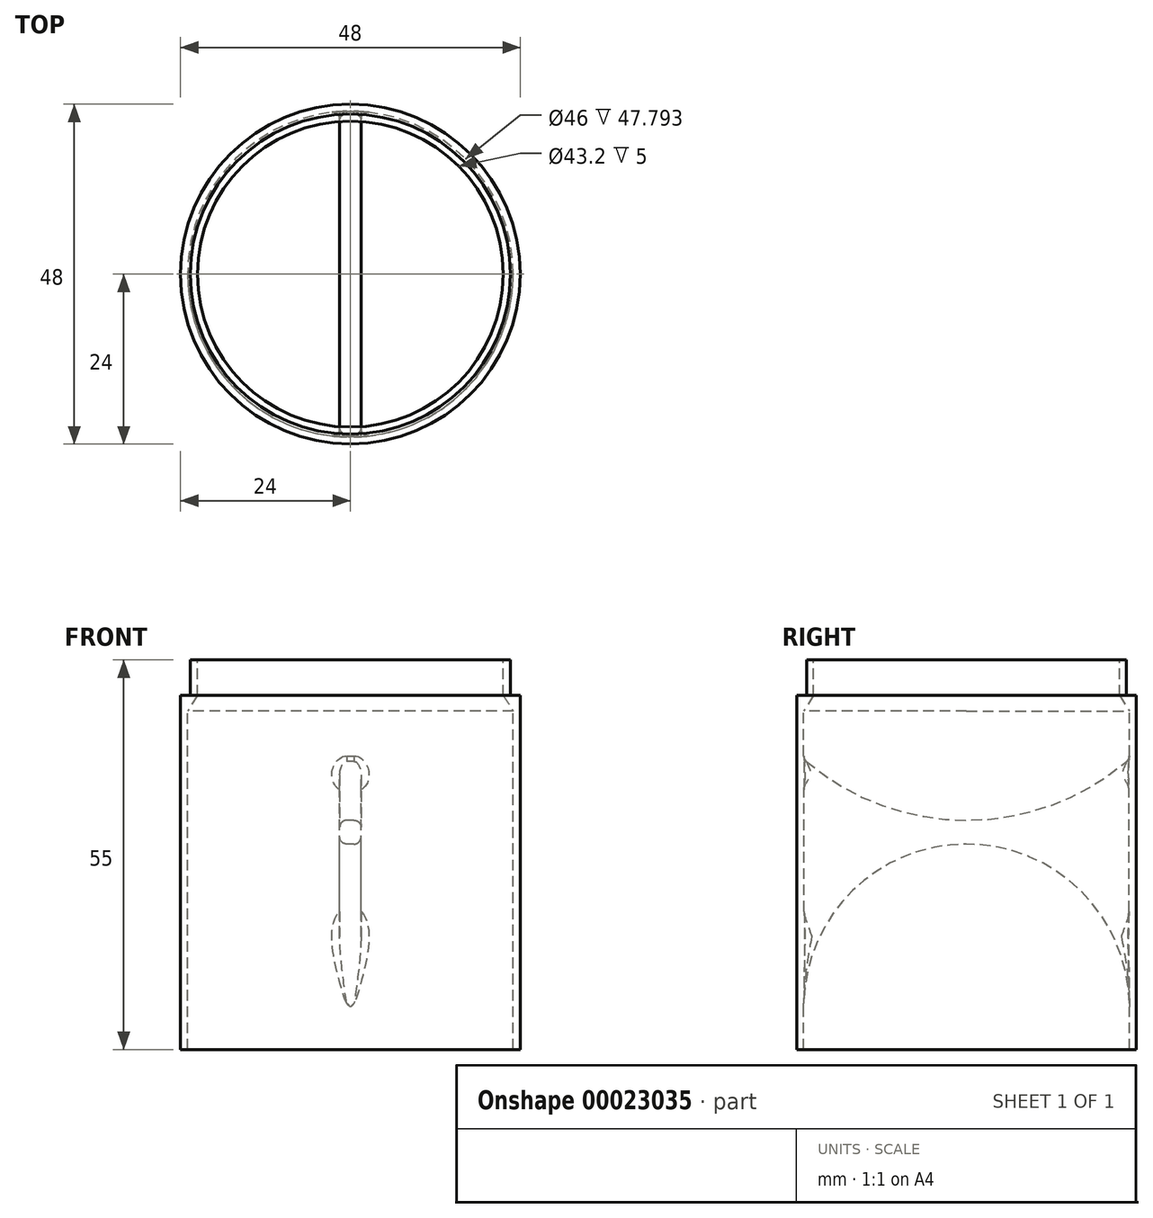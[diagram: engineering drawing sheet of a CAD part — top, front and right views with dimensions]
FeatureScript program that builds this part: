
annotation { "Feature Type Name" : "Feature", "Feature Type Description" : "" }
export const myFeature = defineFeature(function(context is Context, id is Id, definition is map)
    precondition{}
    {
        {
            var Q0;
            Q0=qCreatedBy(makeId("Top.planeOp"),FACE);
            var sketch = newSketch(context, id + "F0", { "sketchPlane" : qUnion([Q0])});
            skCircle(sketch, "E0", {"center": v(0, 0) * mm, "radius": 24 * mm});
            skSolve(sketch);
        }
        {
            var Q0;
            Q0=makeQuery(id+"F0.imprint","IMPRINT",FACE,{"disambiguationData":[TD([[makeQuery(id+"F0.imprint","IMPRINT",EDGE,{"derivedFrom":sQuery(id+"F0.wireOp",EDGE,"E0")}),1.0]])]});
            extrude(context, id + "F1", {"entities" : qUnion([Q0]), "depth" : 50 * mm});
        }
        {
            var Q0;
            Q0=makeQuery(id+"F1.opExtrude","CAP_FACE",FACE,{"disambiguationData":[OSD([sQuery(id+"F0.wireOp",EDGE,"E0")])],"isStart":false});
            var sketch = newSketch(context, id + "F2", { "sketchPlane" : qUnion([Q0])});
            skCircle(sketch, "E1", {"center": v(0, 0) * mm, "radius": 23 * mm});
            skSolve(sketch);
        }
        {
            var Q0;
            Q0=qSketchRegion(id+"F2",true);
            extrude(context, id + "F3", {"entities" : qUnion([Q0]), "operationType" : NewBodyOperationType.REMOVE, "endBound" : BoundingType.THROUGH_ALL, "oppositeDirection" : true, "depth" : 25 * mm});
        }
        {
            var Q0;
            Q0=qCreatedBy(makeId("Front.planeOp"),FACE);
            var sketch = newSketch(context, id + "F4", { "sketchPlane" : qUnion([Q0])});
            skLineSegment(sketch, "E2", {"start": v(0, 0) * mm, "end": v(0, 50) * mm});
            skLineSegment(sketch, "E3.0", {"start": v(-23.5, 50) * mm, "end": v(-23.5, 47) * mm});
            skLineSegment(sketch, "E4", {"start": v(-23.5, 50) * mm, "end": v(-22.6, 50) * mm});
            skLineSegment(sketch, "E5", {"start": v(-22.6, 50) * mm, "end": v(-22.6, 55) * mm});
            skLineSegment(sketch, "E6", {"start": v(-22.6, 55) * mm, "end": v(-21.6, 55) * mm});
            skLineSegment(sketch, "E7", {"start": v(-21.6, 55) * mm, "end": v(-21.6, 50) * mm});
            skLineSegment(sketch, "E8", {"start": v(-21.6, 50) * mm, "end": v(-23.5, 47) * mm});
            skLineSegment(sketch, "E9", {"start": v(-24, 50) * mm, "end": v(-23.5, 50) * mm});
            skSolve(sketch);
        }
        {
            var Q0;
            Q0=qSketchRegion(id+"F4",true);
            var Q1;
            Q1=makeQuery(id+"F3.boolean.opBoolean","COPY",FACE,{"derivedFrom":makeQuery(id+"F3.opExtrude","SWEPT_FACE",FACE,{"disambiguationData":[OSD([sQuery(id+"F2.wireOp",EDGE,"E1")])]})});
            revolve(context, id + "F5", {"operationType" : NewBodyOperationType.ADD, "entities" : qUnion([Q0]), "axis" : qUnion([Q1]), "revolveType" : RevolveType.FULL});
        }
        {
            var Q0;
            Q0=qCreatedBy(makeId("Right.planeOp"),FACE);
            var sketch = newSketch(context, id + "F6", { "sketchPlane" : qUnion([Q0])});
            skCircle(sketch, "E10", {"center": v(0, 27.55) * mm, "radius": 3 * mm});
            skLineSegment(sketch, "E11.rect.bottom", {"start": v(-3, 21.55) * mm, "end": v(3, 21.55) * mm});
            skLineSegment(sketch, "E11.rect.top", {"start": v(-3, 27.55) * mm, "end": v(3, 27.55) * mm});
            skLineSegment(sketch, "E11.rect.left", {"start": v(-3, 21.55) * mm, "end": v(-3, 27.55) * mm});
            skLineSegment(sketch, "E11.rect.right", {"start": v(3, 21.55) * mm, "end": v(3, 27.55) * mm});
            skPoint(sketch, "E11.rect.middle", {"position": v(0, 24.55) * mm});
            skSolve(sketch);
        }
        {
            var Q0;
            Q0=qCreatedBy(makeId("Right.planeOp"),FACE);
            var sketch = newSketch(context, id + "F7", { "sketchPlane" : qUnion([Q0])});
            skLineSegment(sketch, "E12", {"start": v(23, 6) * mm, "end": v(23, 41) * mm});
            skLineSegment(sketch, "E13", {"start": v(0, 5.57) * mm, "end": v(0, 12.96) * mm});
            skLineSegment(sketch, "E14.MirrorCS", {"start": v(-23, 6) * mm, "end": v(-23, 41) * mm});
            skArc(sketch, "E15", {"start": v(23, 6) * mm, "mid": v(0, 29) * mm, "end": v(-23, 6) * mm});
            skLineSegment(sketch, "E16", {"start": v(-23, 6) * mm, "end": v(23, 6) * mm, "construction": true});
            skArc(sketch, "E17", {"start": v(-23, 41) * mm, "mid": v(0, 32.38) * mm, "end": v(23, 41) * mm});
            skSolve(sketch);
        }
        {
            var Q0;
            Q0=qSketchRegion(id+"F7",true);
            extrude(context, id + "F8", {"entities" : qUnion([Q0]), "operationType" : NewBodyOperationType.ADD, "depth" : 1.5 * mm, "hasSecondDirection" : true, "secondDirectionOppositeDirection" : true, "secondDirectionDepth" : 1.5 * mm});
        }
        {
            var Q0;
            Q0=makeQuery(id+"F8.opExtrude","SWEPT_FACE",FACE,{"disambiguationData":[OSD([sQuery(id+"F7.wireOp",EDGE,"39af42c7-0b9f-48d5-9eda-fad9e2f8fca1")])]});
            var Q1;
            Q1=makeQuery(id+"F8.opExtrude","SWEPT_FACE",FACE,{"disambiguationData":[OSD([sQuery(id+"F7.wireOp",EDGE,"E15")])]});
            var Q2;
            Q2=makeQuery(id+"F8.opExtrude","SWEPT_FACE",FACE,{"disambiguationData":[OSD([sQuery(id+"F7.wireOp",EDGE,"E17")])]});
            fillet(context, id + "F9", {"entities" : qUnion([Q0, Q1, Q2]), "radius" : 1 * mm, "tangentPropagation" : true, "allowEdgeOverflow" : false});
        }
    });
